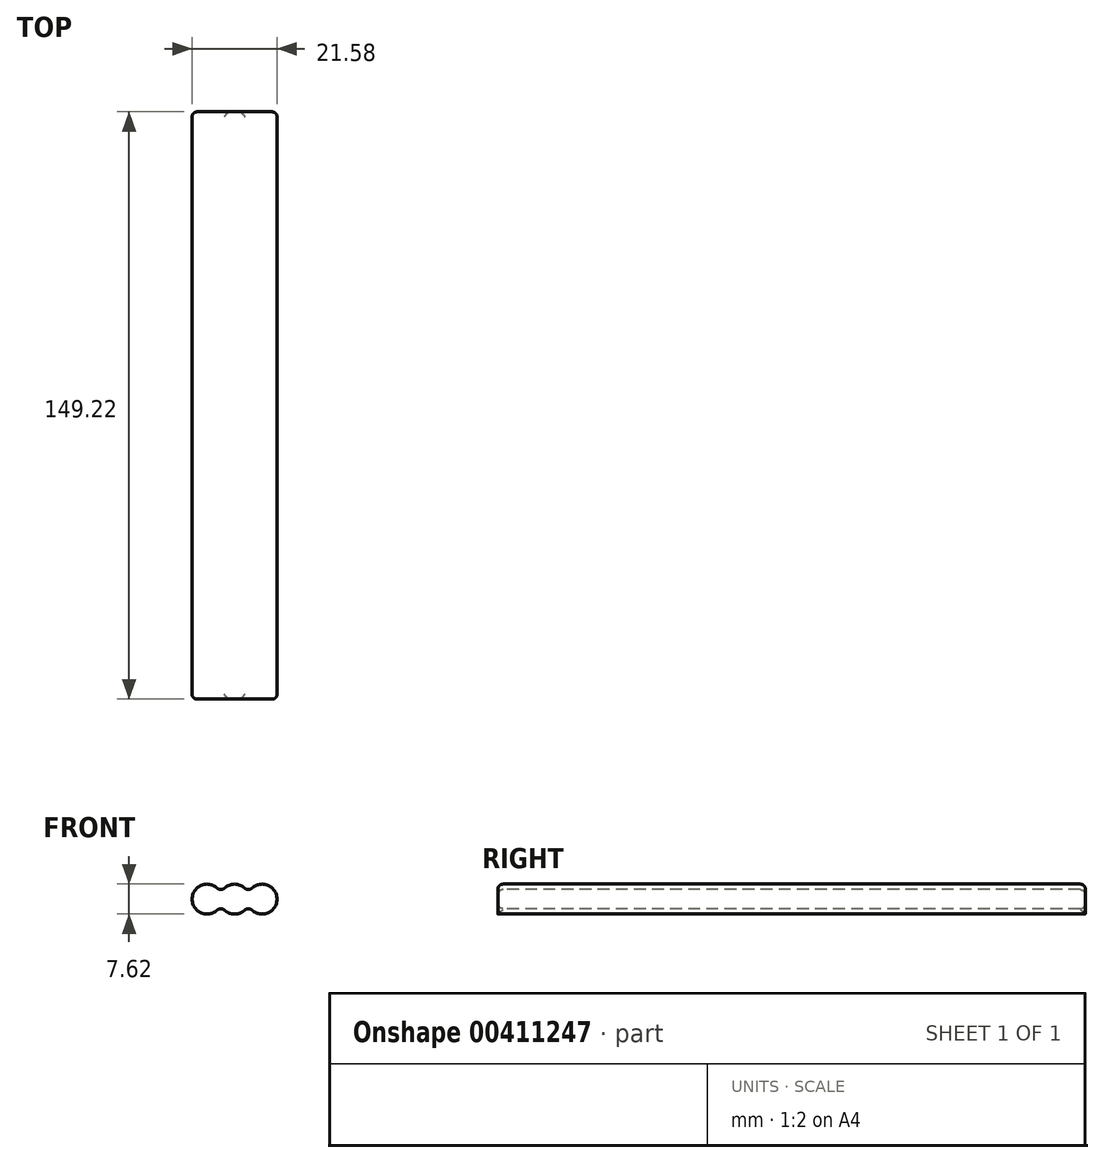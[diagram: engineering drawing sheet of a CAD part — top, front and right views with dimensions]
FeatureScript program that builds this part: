
annotation { "Feature Type Name" : "Feature", "Feature Type Description" : "" }
export const myFeature = defineFeature(function(context is Context, id is Id, definition is map)
    precondition{}
    {
        {
            var Q0;
            Q0=qCreatedBy(makeId("Front.planeOp"),FACE);
            var sketch = newSketch(context, id + "F0", { "sketchPlane" : qUnion([Q0])});
            skArc(sketch, "E0", {"start": v(3.5, 1.52) * mm, "mid": v(0, 3.81) * mm, "end": v(-3.5, 1.52) * mm});
            skArc(sketch, "E1", {"start": v(-3.5, 1.52) * mm, "mid": v(-10.8, 0) * mm, "end": v(-3.5, -1.52) * mm});
            skArc(sketch, "E2", {"start": v(3.5, -1.52) * mm, "mid": v(10.8, 0) * mm, "end": v(3.5, 1.52) * mm});
            skLineSegment(sketch, "E3", {"start": v(-6.99, 0) * mm, "end": v(6.99, 0) * mm, "construction": true});
            skArc(sketch, "E4.trimOffspring", {"start": v(-3.5, -1.52) * mm, "mid": v(0, -3.81) * mm, "end": v(3.5, -1.52) * mm});
            skSolve(sketch);
        }
        {
            var Q0;
            Q0=makeQuery(id+"F0.imprint","IMPRINT",FACE,{"disambiguationData":[TD([[makeQuery(id+"F0.imprint","IMPRINT",EDGE,{"derivedFrom":sQuery(id+"F0.wireOp",EDGE,"E0")}),1.0]])]});
            extrude(context, id + "F1", {"entities" : qUnion([Q0]), "endBound" : BoundingType.SYMMETRIC, "depth" : 149.22 * mm});
        }
        {
            var Q0;
            Q0=makeQuery(id+"F1.opExtrude","SWEPT_FACE",FACE,{"disambiguationData":[OSD([sQuery(id+"F0.wireOp",EDGE,"E2")])]});
            var Q1;
            Q1=makeQuery(id+"F1.opExtrude","SWEPT_FACE",FACE,{"disambiguationData":[OSD([sQuery(id+"F0.wireOp",EDGE,"E0")])]});
            var Q2;
            Q2=makeQuery(id+"F1.opExtrude","SWEPT_FACE",FACE,{"disambiguationData":[OSD([sQuery(id+"F0.wireOp",EDGE,"E1")])]});
            fillet(context, id + "F2", {"entities" : qUnion([Q0, Q1, Q2]), "radius" : 1.27 * mm, "tangentPropagation" : true, "allowEdgeOverflow" : false});
        }
    });
